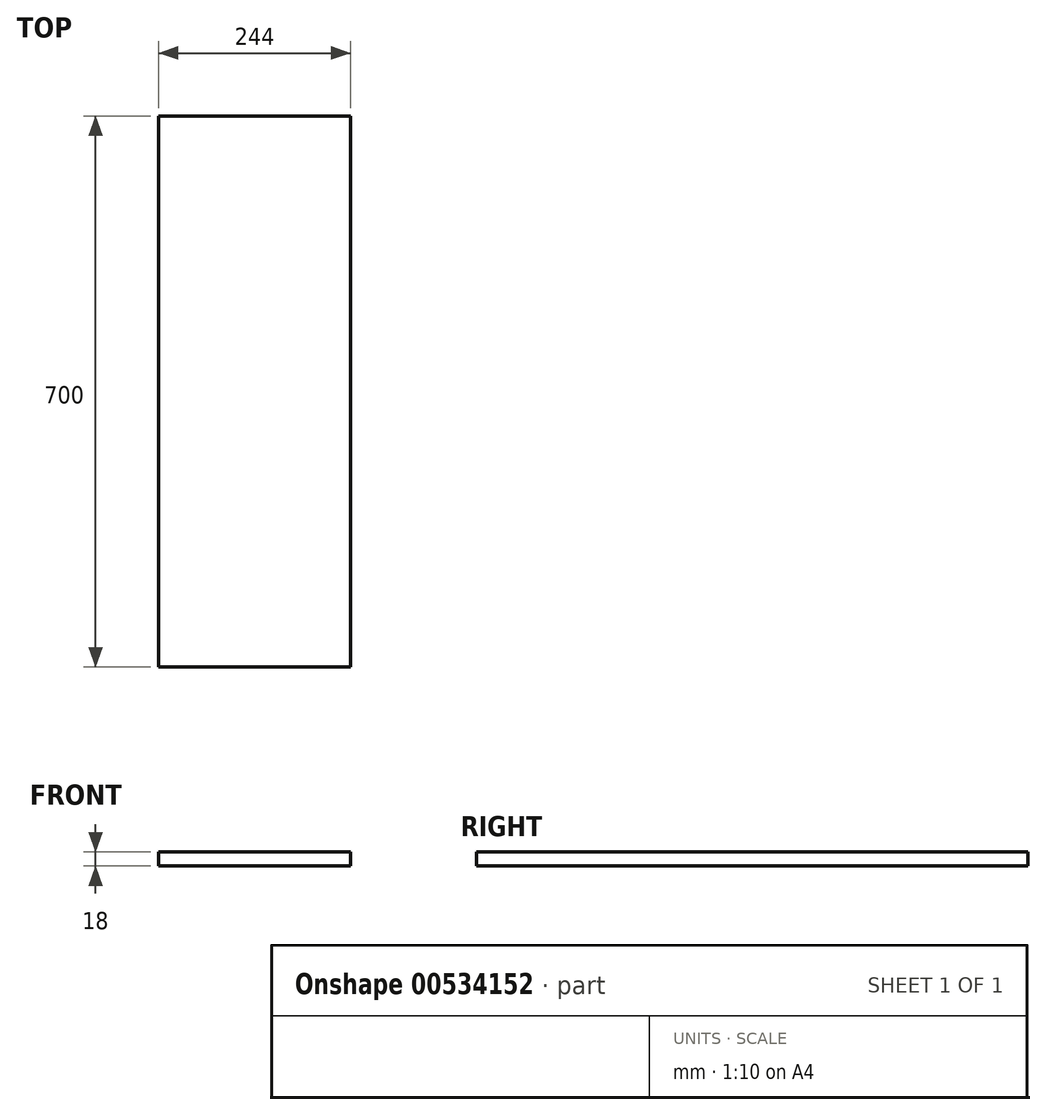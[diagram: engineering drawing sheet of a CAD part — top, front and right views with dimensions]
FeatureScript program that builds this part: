
annotation { "Feature Type Name" : "Feature", "Feature Type Description" : "" }
export const myFeature = defineFeature(function(context is Context, id is Id, definition is map)
    precondition{}
    {
        {
            var Q0;
            Q0=qCreatedBy(makeId("Top.planeOp"),FACE);
            var sketch = newSketch(context, id + "F0", { "sketchPlane" : qUnion([Q0])});
            skLineSegment(sketch, "E0.bottom", {"start": v(0, 0) * mm, "end": v(244, 0) * mm});
            skLineSegment(sketch, "E0.top", {"start": v(0, 700) * mm, "end": v(244, 700) * mm});
            skLineSegment(sketch, "E0.left", {"start": v(0, 0) * mm, "end": v(0, 700) * mm});
            skLineSegment(sketch, "E0.right", {"start": v(244, 0) * mm, "end": v(244, 700) * mm});
            skSolve(sketch);
        }
        {
            var Q0;
            Q0 = qSketchRegion(id + "F0", true);
            extrude(context, id + "F1", {"entities" : qUnion([Q0]), "depth" : 18 * mm, "offsetDistance" : 25 * mm});
        }
    });
